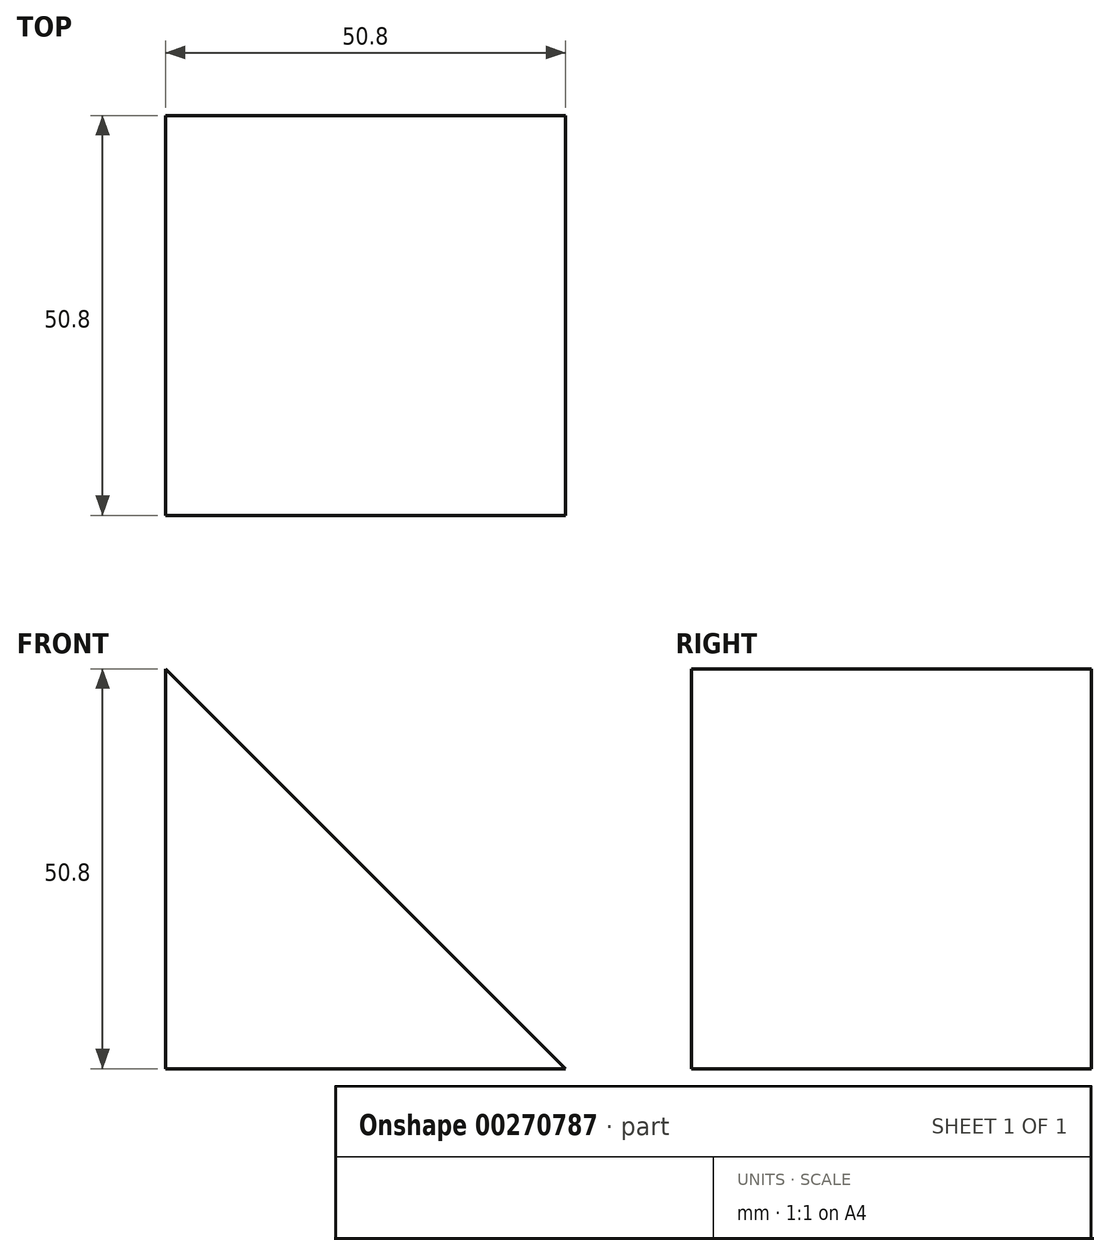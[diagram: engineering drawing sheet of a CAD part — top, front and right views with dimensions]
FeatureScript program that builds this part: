
annotation { "Feature Type Name" : "Feature", "Feature Type Description" : "" }
export const myFeature = defineFeature(function(context is Context, id is Id, definition is map)
    precondition{}
    {
        {
            var Q0;
            Q0=qCreatedBy(makeId("Front.planeOp"),FACE);
            var sketch = newSketch(context, id + "F0", { "sketchPlane" : qUnion([Q0])});
            skLineSegment(sketch, "E0", {"start": v(-52.7, 17.2) * mm, "end": v(-52.7, -33.6) * mm});
            skLineSegment(sketch, "E1", {"start": v(-52.7, -33.6) * mm, "end": v(-1.9, -33.6) * mm});
            skLineSegment(sketch, "E2", {"start": v(-1.9, -33.6) * mm, "end": v(-52.7, 17.2) * mm});
            skSolve(sketch);
        }
        {
            var Q0;
            Q0 = qSketchRegion(id + "F0", true);
            extrude(context, id + "F1", {"entities" : qUnion([Q0]), "depth" : 50.8 * mm});
        }
    });
